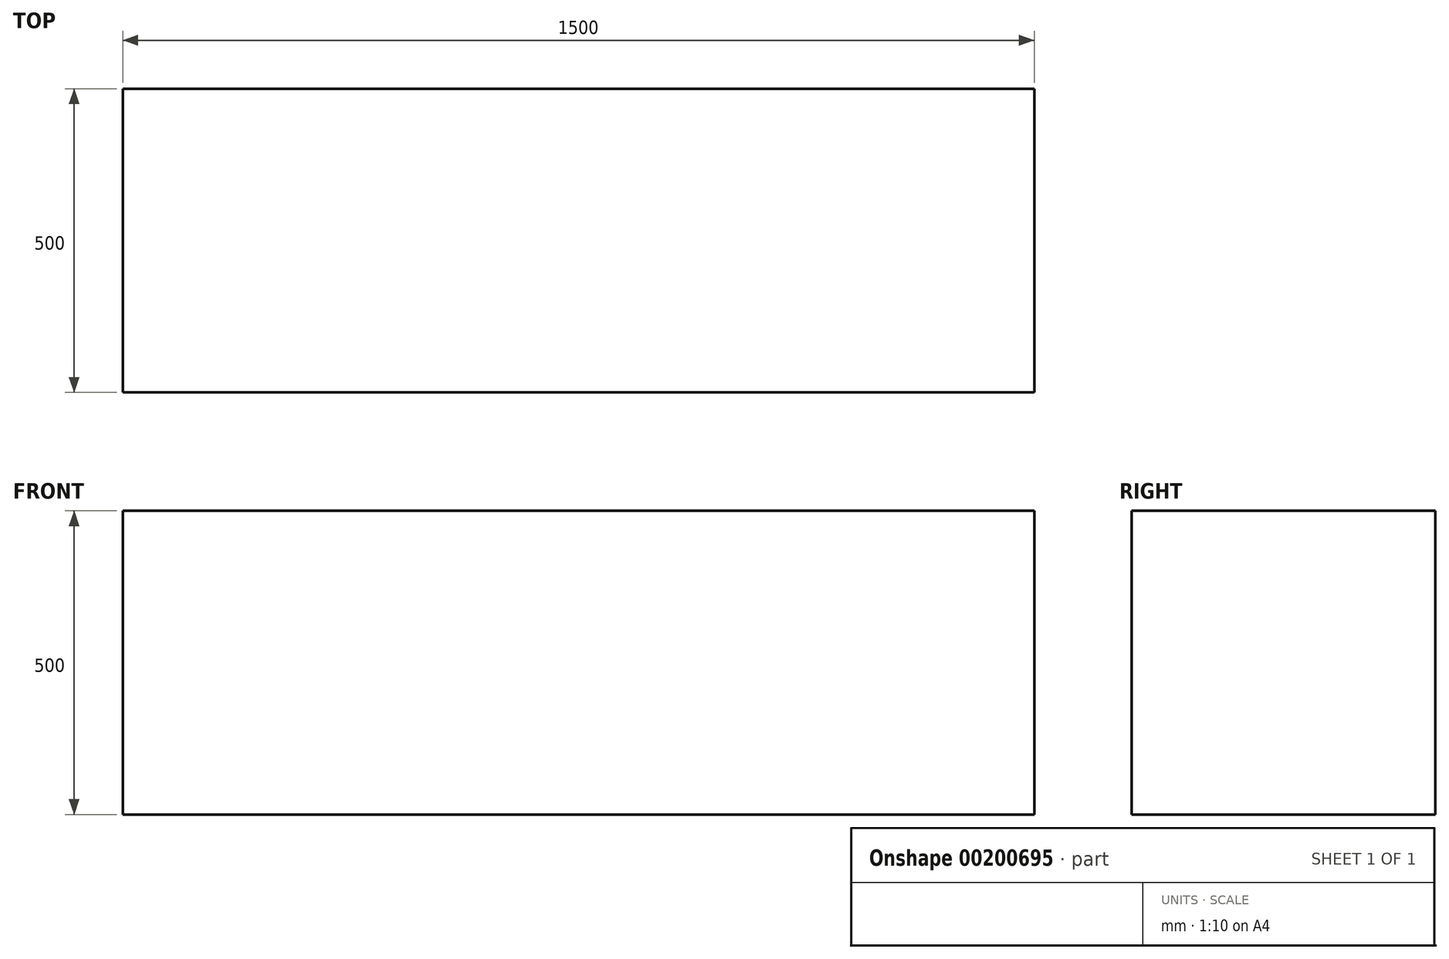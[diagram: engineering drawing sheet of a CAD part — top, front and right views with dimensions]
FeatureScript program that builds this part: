
annotation { "Feature Type Name" : "Feature", "Feature Type Description" : "" }
export const myFeature = defineFeature(function(context is Context, id is Id, definition is map)
    precondition{}
    {
        {
            var Q0;
            Q0=qCreatedBy(makeId("Front.planeOp"),FACE);
            var sketch = newSketch(context, id + "F0", { "sketchPlane" : qUnion([Q0])});
            skLineSegment(sketch, "E0.bottom", {"start": v(0, 0) * mm, "end": v(1500, 0) * mm});
            skLineSegment(sketch, "E0.top", {"start": v(0, 500) * mm, "end": v(1500, 500) * mm});
            skLineSegment(sketch, "E0.left", {"start": v(0, 0) * mm, "end": v(0, 500) * mm});
            skLineSegment(sketch, "E0.right", {"start": v(1500, 0) * mm, "end": v(1500, 500) * mm});
            skSolve(sketch);
        }
        {
            var Q0;
            Q0=qSketchRegion(id+"F0",true);
            extrude(context, id + "F1", {"entities" : qUnion([Q0]), "depth" : 500 * mm});
        }
    });
